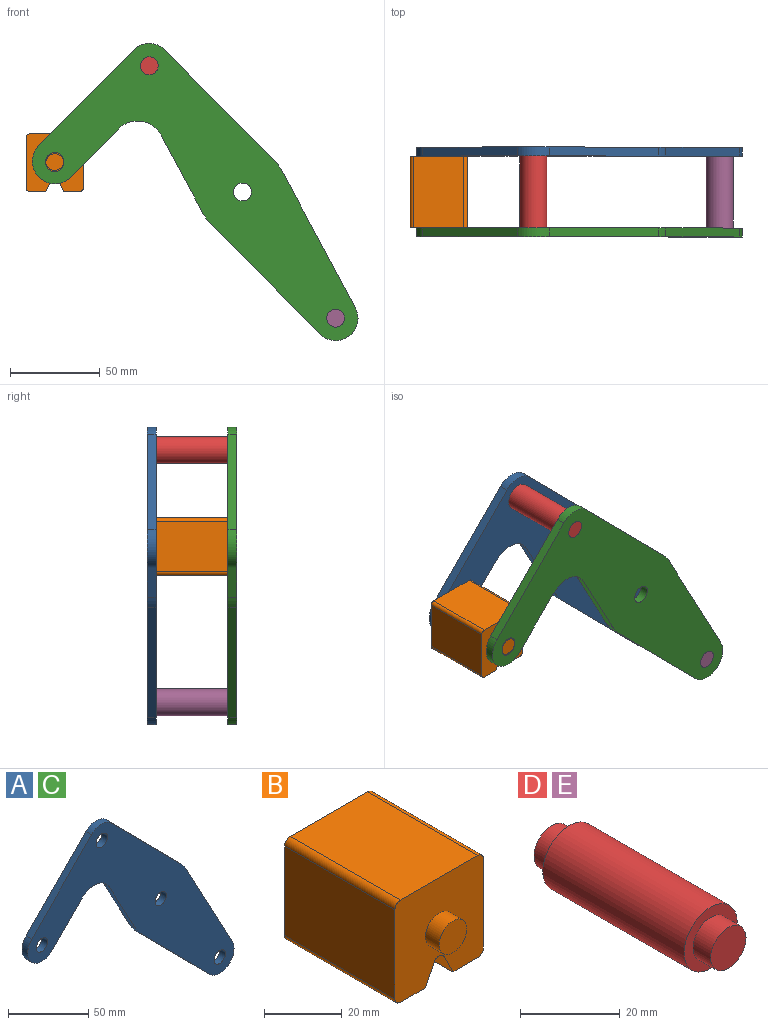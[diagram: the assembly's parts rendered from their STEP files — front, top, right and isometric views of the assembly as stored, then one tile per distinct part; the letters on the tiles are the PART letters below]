
ASSEMBLY  parts=5 mates=3
PART A: 18 faces, bbox 181.7x5x165.8 mm
  f0: plane 43.49x23.35mm, normal (-0.88,0,-0.47), area 246.8mm2, adj f1,f14,f16,f17
  f1: cylinder r=25mm len=5.75mm, axis (0,1,0), area 35.8mm2, adj f0,f2,f16,f17
  f2: plane 61.6x60.87mm, normal (-0.71,0,-0.7), area 433mm2, adj f1,f3,f16,f17
  f3: cylinder r=12.5mm len=21.39mm, axis (0,1,0), area 178.4mm2, adj f2,f4,f16,f17
  f4: plane 76.3x40.96mm, normal (0.88,0,0.47), area 433mm2, adj f3,f5,f16,f17
  f5: cylinder r=25mm len=5.75mm, axis (0,1,0), area 35.8mm2, adj f4,f6,f16,f17
  f6: plane 61.6x60.87mm, normal (0.71,0,0.7), area 433mm2, adj f5,f7,f16,f17
  f7: cylinder r=12.5mm len=17.78mm, axis (0,1,0), area 98.9mm2, adj f6,f8,f16,f17
  f8: plane 53.35x52.71mm, normal (-0.71,0,0.7), area 375mm2, adj f7,f9,f16,f17
  f9: cylinder r=12.5mm len=21.39mm, axis (0,1,0), area 196.3mm2, adj f8,f10,f16,f17
  f10: plane 26.86x26.54mm, normal (0.71,0,-0.7), area 188.8mm2, adj f9,f14,f16,f17
  f11: cylinder r=5mm len=10mm, axis (0,1,0), area 157.1mm2, adj f16,f17
  f12: cylinder r=5mm len=10mm, axis (0,1,0), area 157.1mm2, adj f16,f17
  f13: cylinder r=5mm len=10mm, axis (0,1,0), area 157.1mm2, adj f16,f17
  f14: cylinder r=15mm len=23.89mm, axis (0,1,0), area 140.2mm2, adj f0,f10,f16,f17
  f15: cylinder r=5mm len=10mm, axis (0,1,0), area 157.1mm2, adj f16,f17
  f16: plane 181.66x165.78mm, normal (0,-1,0), area 8710.1mm2, adj f0,f1,f2,f3,f4,f5,f6,f7
  f17: plane 181.66x165.78mm, normal (0,1,0), area 8710.1mm2, adj f0,f1,f2,f3,f4,f5,f6,f7
PART B: 18 faces, bbox 32.1x50x32.1 mm
  f0: plane 40x28.08mm, normal (1,0,0), area 1123.1mm2, adj f4,f10,f13,f14
  f1: plane 40x9.04mm, normal (0,0,-1), area 361.6mm2, adj f2,f4,f10,f14
  f2: plane 40x6.42mm, normal (-0.89,0,-0.45), area 287.2mm2, adj f1,f4,f10,f15
  f3: plane 40x6.42mm, normal (0.89,0,-0.45), area 287.2mm2, adj f4,f5,f10,f15
  f4: plane 32.08x32.08mm, normal (0,-1,0), area 900.6mm2, adj f0,f1,f2,f3,f5,f6,f7,f9
  f5: plane 40x9.04mm, normal (0,0,-1), area 361.6mm2, adj f3,f4,f10,f16
  f6: plane 40x28.08mm, normal (0,0,1), area 1123.1mm2, adj f4,f10,f13,f17
  f7: plane 40x28.08mm, normal (-1,0,0), area 1123.1mm2, adj f4,f10,f16,f17
  f8: plane 10x10mm, normal (0,-1,0), area 78.5mm2, adj f9
  f9: cylinder r=5mm len=10mm, axis (0,1,0), area 157.1mm2, adj f4,f8
  f10: plane 32.08x32.08mm, normal (0,1,0), area 900.6mm2, adj f0,f1,f2,f3,f5,f6,f7,f12
  f11: plane 10x10mm, normal (0,1,0), area 78.5mm2, adj f12
  f12: cylinder r=5mm len=10mm, axis (0,-1,0), area 157.1mm2, adj f10,f11
  f13: cylinder r=2mm len=40mm, axis (0,1,0), area 125.7mm2, adj f0,f4,f6,f10
  f14: cylinder r=2mm len=40mm, axis (0,-1,0), area 125.7mm2, adj f0,f1,f4,f10
  f15: cylinder r=2mm len=40mm, axis (0,1,0), area 177.1mm2, adj f2,f3,f4,f10
  f16: cylinder r=2mm len=40mm, axis (0,1,0), area 125.7mm2, adj f4,f5,f7,f10
  f17: cylinder r=2mm len=40mm, axis (0,-1,0), area 125.7mm2, adj f4,f6,f7,f10
PART C: same geometry as A
PART D: 7 faces, bbox 15x50x15 mm
  f0: cylinder r=7.5mm len=40mm, axis (0,-1,0), area 1885mm2, adj f2,f5
  f1: cylinder r=5mm len=10mm, axis (0,1,0), area 157.1mm2, adj f2,f3
  f2: plane 15x15mm, normal (0,-1,0), area 98.2mm2, adj f0,f1
  f3: plane 10x10mm, normal (0,-1,0), area 78.5mm2, adj f1
  f4: cylinder r=5mm len=10mm, axis (0,-1,0), area 157.1mm2, adj f5,f6
  f5: plane 15x15mm, normal (0,1,0), area 98.2mm2, adj f0,f4
  f6: plane 10x10mm, normal (0,1,0), area 78.5mm2, adj f4
PART E: same geometry as D
PLACE A t=(0,25,0)mm
PLACE B t=(0,-20,-0.67)mm
PLACE C t=(0,-20,0)mm fixed
PLACE D t=(0,-20,0)mm
PLACE E t=(103.95,-20,-140.78)mm
MATE fastened D.f0 <-> A.f7  axis (0,1,0) through (-51.98,20,70.39)mm
MATE revolute B.f4 <-> C.f9  axis (0,-1,0) through (-104.69,-20,17.04)mm
MATE fastened E.f0 <-> C.f3  axis (0,-1,0) through (51.98,-20,-70.39)mm
